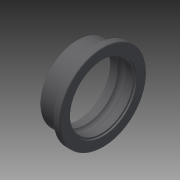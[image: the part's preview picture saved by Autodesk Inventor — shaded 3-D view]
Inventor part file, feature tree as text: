
AUTODESK INVENTOR PART (.ipt)
format: ipt  version: 2014 SP2 (Build 180246200, 246)  size: 157,184 bytes
history: native  units: mm
features: other x14, revolve x1, sketch x1
ambient origin geometry x8: Origin, YZ Plane, XZ Plane, XY Plane, X Axis, Y Axis, Z Axis, Center Point
bodies: Solid1 (feature_tree)
feature tree (16):
  revolve  "Revolution1"  [1 undecoded]
  other  "ip_st_1_XY"
  other  "ip_st_1_YZ"
  other  "ip_st_1_ZX"
  other  "ip_st_1_X"
  other  "ip_st_1_Y"
  other  "ip_st_1_Z"
  other  "ip_st_1_Center"
  other  "ip_st_2_XY"
  other  "ip_st_2_YZ"
  other  "ip_st_2_ZX"
  other  "ip_st_2_X"
  other  "ip_st_2_Y"
  other  "ip_st_2_Z"
  other  "ip_st_2_Center"
  sketch  "Sketch_1"  dims[d0=360.0deg d1=0.0mm d2=0.0mm]
note: 1 required parameter value undecoded (feature->parameter linkage not recoverable at this tier; creation-order binding heuristic only, values carry confidence <= 0.55)
